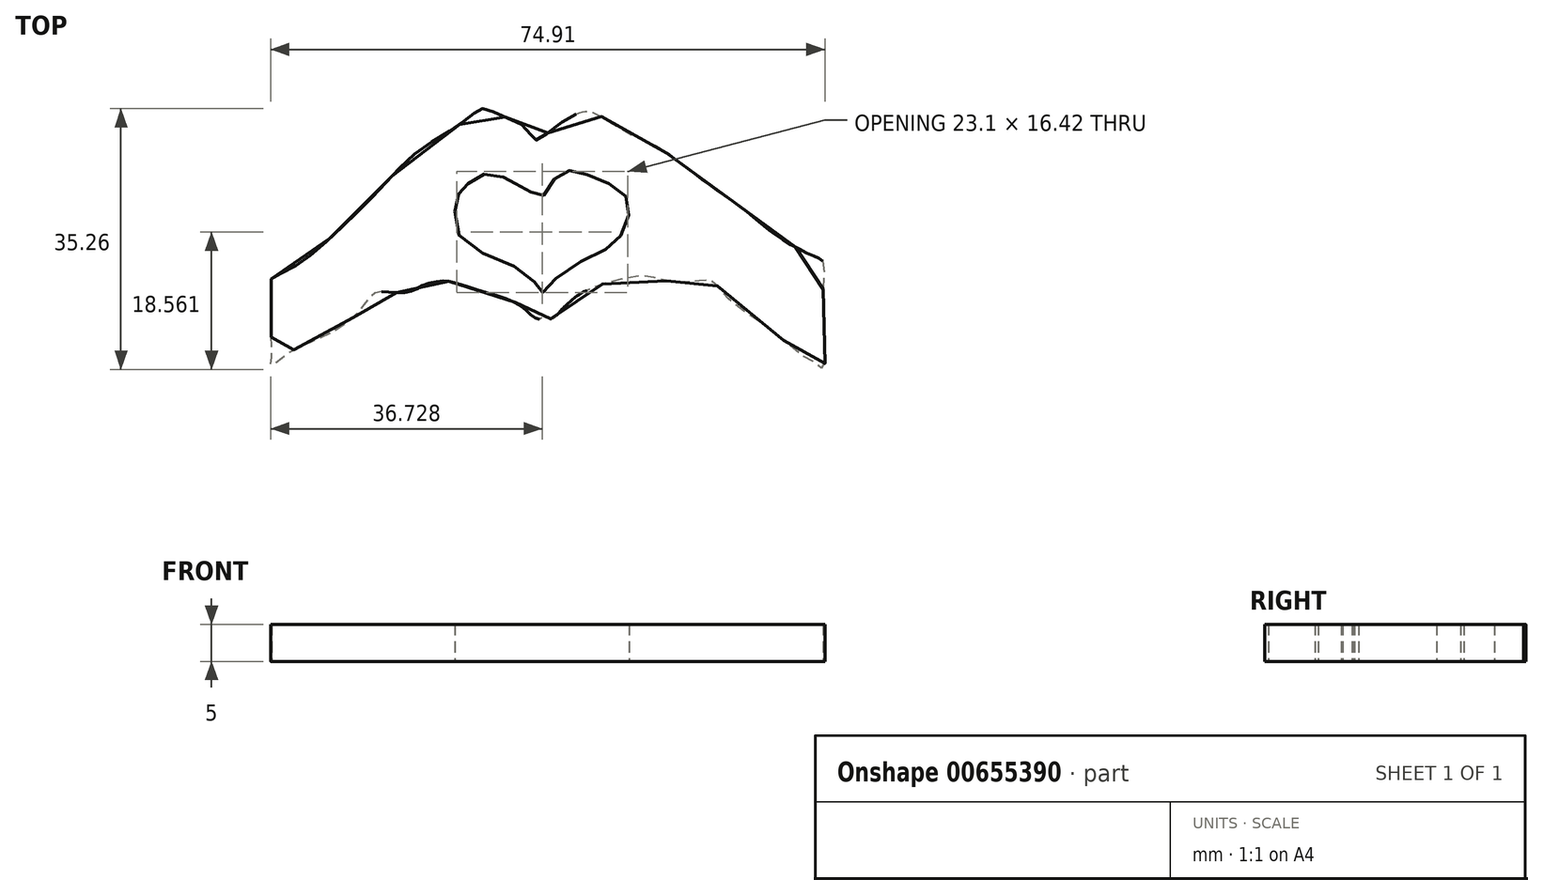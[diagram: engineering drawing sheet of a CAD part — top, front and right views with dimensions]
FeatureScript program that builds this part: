
annotation { "Feature Type Name" : "Feature", "Feature Type Description" : "" }
export const myFeature = defineFeature(function(context is Context, id is Id, definition is map)
    precondition{}
    {
        {
            var Q0;
            Q0=qCreatedBy(makeId("Top.planeOp"),FACE);
            var sketch = newSketch(context, id + "F0", { "sketchPlane" : qUnion([Q0])});
            skFitSpline(sketch, "E0", {"points": [v(-74.63, 31.44) * mm, v(-72.58, 32.52) * mm, v(-68.55, 35.3) * mm, v(-63.37, 40.11) * mm, v(-59.02, 44.57) * mm, v(-54.57, 48.9) * mm, v(-49.32, 52.21) * mm, v(-47.1, 53.98) * mm, v(-45.87, 54.47) * mm, v(-43.65, 53.57) * mm, v(-40.34, 51.94) * mm, v(-39.12, 50.31) * mm, v(-38.53, 50.31) * mm, v(-34.95, 52.9) * mm, v(-32.36, 54.07) * mm, v(-31.18, 53.98) * mm, v(-26.02, 51) * mm, v(-22.89, 49.59) * mm, v(-19.04, 46.87) * mm, v(-14.28, 43.37) * mm, v(-9.52, 39.84) * mm, v(-6.66, 37.53) * mm, v(-1.72, 34.72) * mm, v(0, 33.69) * mm, v(0, 31.3) * mm, v(0, 27.89) * mm, v(0, 23.82) * mm, v(0, 19.21) * mm, v(-0.93, 20.05) * mm, v(-1.95, 20.46) * mm, v(-7.4, 24.79) * mm, v(-13.04, 28.9) * mm, v(-14.72, 30.94) * mm, v(-15.89, 31.3) * mm, v(-18.38, 31) * mm, v(-21.9, 31.35) * mm, v(-24.13, 31.86) * mm, v(-28.46, 31.15) * mm, v(-32.88, 29.42) * mm, v(-35.94, 26.67) * mm, v(-36.8, 26) * mm, v(-37.77, 26.41) * mm, v(-38.33, 26) * mm, v(-39.55, 26.62) * mm, v(-41.38, 28.1) * mm, v(-46.31, 29.82) * mm, v(-49.83, 30.94) * mm, v(-51.66, 31.15) * mm, v(-54.35, 30.46) * mm, v(-56.33, 29.6) * mm, v(-59.6, 29.74) * mm, v(-60.97, 29.3) * mm, v(-62.63, 27.3) * mm, v(-65.1, 25.02) * mm, v(-69.25, 22.9) * mm, v(-72.16, 21.5) * mm, v(-74.63, 19.7) * mm, v(-74.63, 20.35) * mm, v(-74.63, 23.8) * mm, v(-74.63, 28.51) * mm, v(-74.63, 30.53) * mm, v(-74.63, 31.44) * mm]});
            skFitSpline(sketch, "E1", {"points": [v(-37.94, 29.56) * mm, v(-35.8, 31.86) * mm, v(-29.95, 35.16) * mm, v(-27.51, 37.14) * mm, v(-26.24, 40.66) * mm, v(-27.05, 43.05) * mm, v(-30.41, 44.98) * mm, v(-33.62, 46) * mm, v(-35.35, 45.85) * mm, v(-37.43, 43.4) * mm, v(-38.25, 42.44) * mm, v(-40.7, 44.01) * mm, v(-42.01, 44.42) * mm, v(-43.39, 45.29) * mm, v(-46.34, 45.49) * mm, v(-48.32, 44.06) * mm, v(-49.29, 43.05) * mm, v(-49.8, 40.86) * mm, v(-48.68, 36.58) * mm, v(-41.5, 32.97) * mm, v(-38.55, 30.33) * mm, v(-37.94, 29.56) * mm]});
            skSolve(sketch);
        }
        {
            var Q0;
            Q0=makeQuery(id+"F0.imprint","IMPRINT",FACE,{"disambiguationData":[TD([[makeQuery(id+"F0.imprint","IMPRINT",EDGE,{"derivedFrom":sQuery(id+"F0.wireOp",EDGE,"E0")}),-1.0]])]});
            extrude(context, id + "F1", {"entities" : qUnion([Q0]), "depth" : 5 * mm, "offsetDistance" : 25.4 * mm});
        }
    });
